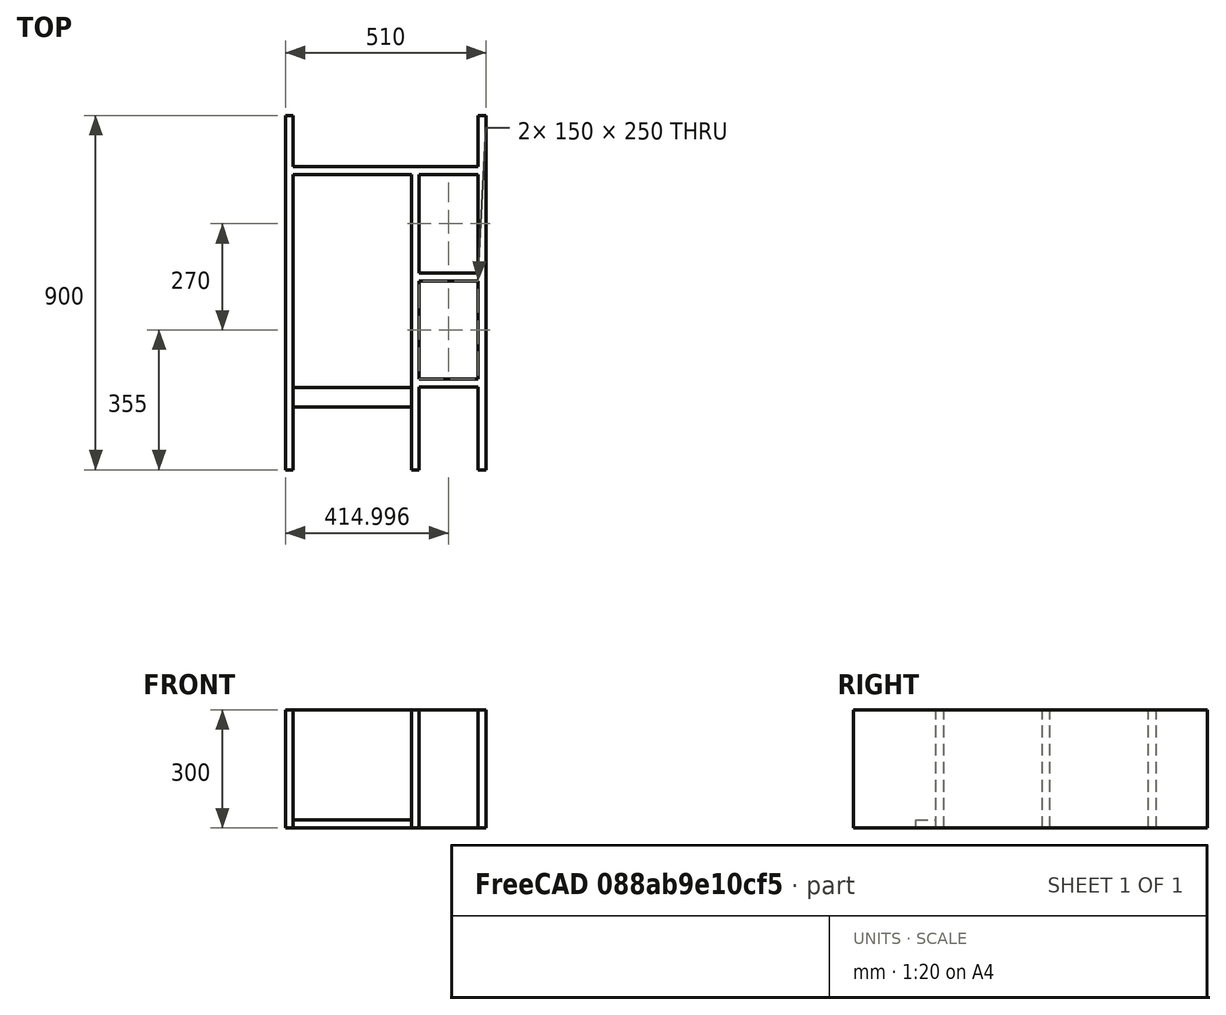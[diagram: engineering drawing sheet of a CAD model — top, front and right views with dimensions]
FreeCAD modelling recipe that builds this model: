
FCSTD DOCUMENT  (FreeCAD 0.18R16110 (Git))
Label: MeubleElodie
License: All rights reserved
LicenseURL: http://en.wikipedia.org/wiki/All_rights_reserved
objects: TechDraw::DrawViewDimension×9, Sketcher::SketchObject×2, PartDesign::Pad×2, TechDraw::DrawSVGTemplate×1, TechDraw::DrawViewAnnotation×1, PartDesign::Body×1, App::Part×1, TechDraw::DrawProjGroupItem×1, TechDraw::DrawProjGroup×1, TechDraw::DrawViewSection×1, TechDraw::DrawViewPart×1, TechDraw::DrawPage×1
note: 7 computed .brp shape members not serialized (recipe doc carries the construction recipe); baked Part::Feature solids carry a one-line shape summary decoded from their .brp

FEATURE [Sketcher::SketchObject] Sketch
  MapMode = 5
  Support = -> [XY_Plane001]
  sketch-geometry (23):
    g0: LineSegment StartX=-287.354 StartY=130 StartZ=0 EndX=-287.354 EndY=-770 EndZ=0
    g1: LineSegment StartX=-287.354 StartY=-770 StartZ=0 EndX=-267.354 EndY=-770 EndZ=0
    g2: LineSegment StartX=-267.354 StartY=-770 StartZ=0 EndX=-267.354 EndY=-20 EndZ=0
    g3: LineSegment StartX=-267.354 StartY=-20 StartZ=0 EndX=32.6459 EndY=-20 EndZ=0
    g4: LineSegment StartX=32.6459 StartY=-20 StartZ=0 EndX=32.6459 EndY=-770 EndZ=0
    g5: LineSegment StartX=32.6459 StartY=-770 StartZ=0 EndX=52.6459 EndY=-770 EndZ=0
    g6: LineSegment StartX=52.6459 StartY=-770 StartZ=0 EndX=52.6459 EndY=-560 EndZ=0
    g7: LineSegment StartX=52.6459 StartY=-20 StartZ=0 EndX=202.646 EndY=-20 EndZ=0
    g8: LineSegment StartX=202.646 StartY=-20 StartZ=0 EndX=202.646 EndY=-770 EndZ=0
    g9: LineSegment StartX=202.646 StartY=-770 StartZ=0 EndX=222.646 EndY=-770 EndZ=0
    g10: LineSegment StartX=222.646 StartY=-770 StartZ=0 EndX=222.646 EndY=130 EndZ=0
    g11: LineSegment StartX=222.646 StartY=130 StartZ=0 EndX=202.646 EndY=130 EndZ=0
    g12: LineSegment StartX=202.646 StartY=130 StartZ=0 EndX=202.646 EndY=0 EndZ=0
    g13: LineSegment StartX=202.646 StartY=0 StartZ=0 EndX=-267.354 EndY=0 EndZ=0
    g14: LineSegment StartX=-267.354 StartY=0 StartZ=0 EndX=-267.354 EndY=130 EndZ=0
    g15: LineSegment StartX=-287.354 StartY=130 StartZ=0 EndX=-267.354 EndY=130 EndZ=0
    g16: LineSegment StartX=52.6459 StartY=-270 StartZ=0 EndX=202.646 EndY=-270 EndZ=0
    g17: LineSegment StartX=202.646 StartY=-290 StartZ=0 EndX=52.6459 EndY=-290 EndZ=0
    g18: LineSegment StartX=52.6459 StartY=-270 StartZ=0 EndX=52.6459 EndY=-20 EndZ=0
    g19: LineSegment StartX=52.6459 StartY=-540 StartZ=0 EndX=202.646 EndY=-540 EndZ=0
    g20: LineSegment StartX=202.646 StartY=-540 StartZ=0 EndX=202.646 EndY=-560 EndZ=0
    g21: LineSegment StartX=202.646 StartY=-560 StartZ=0 EndX=52.6459 EndY=-560 EndZ=0
    g22: LineSegment StartX=52.6459 StartY=-540 StartZ=0 EndX=52.6459 EndY=-290 EndZ=0
  constraints (67):
    c: Coincident(g0,g1)
    c: Coincident(g1,g2)
    c: Vertical(g2)
    c: Coincident(g2,g3)
    c: Horizontal(g3)
    c: Coincident(g3,g4)
    c: Vertical(g4)
    c: Coincident(g4,g5)
    c: Horizontal(g5)
    c: Coincident(g5,g6)
    c: Vertical(g6)
    c: Coincident(g18,g7)
    c: Horizontal(g7)
    c: Coincident(g7,g8)
    c: Vertical(g8)
    c: Coincident(g8,g9)
    c: Horizontal(g9)
    c: Coincident(g9,g10)
    c: Vertical(g10)
    c: Coincident(g10,g11)
    c: Coincident(g11,g12)
    c: PointOnObject(g12,g-1)
    c: Vertical(g12)
    c: Coincident(g12,g13)
    c: PointOnObject(g13,g-1)
    c: Coincident(g13,g14)
    c: Vertical(g14)
    c: Horizontal(g11)
    c: Equal(g14,g12)
    c: Equal(g10,g0)
    c: Equal(g2,g4)
    c: Equal(g4,g8)
    c: DistanceY(g2,g2) = 750
    c: DistanceX(g0,g1) = 20
    c: DistanceY(g7,g12) = 20
    c: Equal(g1,g5)
    c: Equal(g5,g9)
    c: Equal(g9,g11)
    c: DistanceY(g2,g14) = 150
    c: Coincident(g15,g0)
    c: Coincident(g15,g14)
    c: Horizontal(g15)
    c: Equal(g15,g11)
    c: Horizontal(g16)
    c: Horizontal(g17)
    c: DistanceY(g17,g16) = 20
    c: Coincident(g18,g16)
    c: Tangent(g6,g18)
    c: Coincident(g22,g17)
    c: PointOnObject(g16,g8)
    c: PointOnObject(g17,g8)
    c: DistanceY(g2,g13) = 20
    c: DistanceX(g0,g10) = 510
    c: DistanceX(g7,g7) = 150
    c: DistanceY(g16,g7) = 250
    c: Coincident(g19,g20)
    c: Coincident(g20,g21)
    c: Horizontal(g19)
    c: Horizontal(g21)
    c: Vertical(g20)
    c: PointOnObject(g20,g8)
    c: DistanceY(g20,g19) = 20
    c: DistanceY(g19,g17) = 250
    c: PointOnObject(g6,g21)
    c: Coincident(g22,g19)
    c: Tangent(g6,g22)
    c: Parallel(g0,g4)
FEATURE [PartDesign::Pad] Pad
  Length = 300
  Length2 = 100
  Profile = -> Sketch
  Type = 0
FEATURE [TechDraw::DrawSVGTemplate] Template
  EditableTexts = Designed_by_Name=Papa d Elodie; Drawing_number=1.0; FC-Date=29/07/2019; FC-SC=1/10; FC-SH=1; FC-Title=Meuble d Elodie; Subtitle=Subtitle
  Height = 210
  Orientation = 1
  Width = 297
FEATURE [TechDraw::DrawViewAnnotation] Annotation
  Font = osifont
  LineSpace = 80
  LockPosition = false
  MaxWidth = -1
  Rotation = 0
  ScaleType = 0
  Text = 2 - 90x30x2 | 1 - 75x30x2  | 2 - 15x30x2 | 1 - 47x30x2 | 1 - 30x5x2
  TextSize = 5
  TextStyle = 0
  X = 238.236
  Y = 98.3941
FEATURE [Sketcher::SketchObject] Sketch001
  ExternalGeometry = -> [Sketch]
  MapMode = 5
  Support = -> [XY_Plane001]
  sketch-geometry (4):
    g0: LineSegment StartX=-267.354 StartY=-560.446 StartZ=0 EndX=32.6459 EndY=-560.446 EndZ=0
    g1: LineSegment StartX=32.6459 StartY=-560.446 StartZ=0 EndX=32.6459 EndY=-610.446 EndZ=0
    g2: LineSegment StartX=32.6459 StartY=-610.446 StartZ=0 EndX=-267.354 EndY=-610.446 EndZ=0
    g3: LineSegment StartX=-267.354 StartY=-610.446 StartZ=0 EndX=-267.354 EndY=-560.446 EndZ=0
  constraints (11):
    c: Coincident(g0,g1)
    c: Coincident(g1,g2)
    c: Coincident(g2,g3)
    c: Coincident(g3,g0)
    c: Horizontal(g0)
    c: Horizontal(g2)
    c: Vertical(g1)
    c: Vertical(g3)
    c: PointOnObject(g0,g-3)
    c: PointOnObject(g1,g-4)
    c: DistanceY(g1,g1) = 50
FEATURE [PartDesign::Pad] Pad001
  BaseFeature = -> Pad
  Length = 20
  Length2 = 100
  Profile = -> Sketch001
  Type = 0
FEATURE [PartDesign::Body] Body
  Group = -> [Sketch,Pad,Sketch001,Pad001]
  Origin = -> Origin001
  Tip = -> Pad001
FEATURE [App::Part] Part
  Group = -> [Body]
  Origin = -> Origin
FEATURE [TechDraw::DrawProjGroupItem] ProjItem005  label="Front001"
  CoarseView = false
  Direction = (0,0,1)
  Focus = 100
  HardHidden = false
  IsoCount = 0
  IsoHidden = false
  IsoVisible = false
  LockPosition = true
  Perspective = false
  Rotation = 0
  RotationVector = (1,0,0)
  Scale = 0.1
  ScaleType = 2
  SeamHidden = false
  SeamVisible = false
  SmoothHidden = false
  SmoothVisible = false
  Source = -> [Pad001]
  Type = 0
  X = 0
  Y = 0
FEATURE [TechDraw::DrawProjGroup] ProjGroup002
  Anchor = -> ProjItem005
  AutoDistribute = true
  LockPosition = false
  ProjectionType = 0
  Rotation = 0
  Scale = 0.1
  ScaleType = 2
  Source = -> [Pad001]
  Views = -> [ProjItem005]
  X = 67.2245
  Y = 133.567
  spacingX = 15
  spacingY = 15
FEATURE [TechDraw::DrawViewDimension] Dimension
  Arbitrary = false
  FormatSpec = %.2f
  LockPosition = false
  MeasureType = 1
  OverTolerance = 0
  References2D = -> [ProjItem005]
  Rotation = 0
  ScaleType = 0
  Type = 2
  UnderTolerance = 0
  X = -44.8231
  Y = -1.12249
FEATURE [TechDraw::DrawViewDimension] Dimension001
  Arbitrary = false
  FormatSpec = %.2f
  LockPosition = false
  MeasureType = 1
  OverTolerance = 0
  References2D = -> [ProjItem005]
  Rotation = 0
  ScaleType = 0
  Type = 2
  UnderTolerance = 0
  X = -11.9088
  Y = -5.70402
FEATURE [TechDraw::DrawViewDimension] Dimension003
  Arbitrary = false
  FormatSpec = %.2f
  LockPosition = false
  MeasureType = 1
  OverTolerance = 0
  References2D = -> [ProjItem005]
  Rotation = 0
  ScaleType = 0
  Type = 1
  UnderTolerance = 0
  X = -2.69397
  Y = 59.5324
FEATURE [TechDraw::DrawViewDimension] Dimension004
  Arbitrary = false
  FormatSpec = %.2f
  LockPosition = false
  MeasureType = 1
  OverTolerance = 0
  References2D = -> [ProjItem005]
  Rotation = 0
  ScaleType = 0
  Type = 1
  UnderTolerance = 0
  X = -43.2957
  Y = -57.1951
FEATURE [TechDraw::DrawViewDimension] Dimension005
  Arbitrary = false
  FormatSpec = %.2f
  LockPosition = false
  MeasureType = 1
  OverTolerance = 0
  References2D = -> [ProjItem005]
  Rotation = 0
  ScaleType = 0
  Type = 1
  UnderTolerance = 0
  X = -2.05828
  Y = -61.5108
FEATURE [TechDraw::DrawViewDimension] Dimension006
  Arbitrary = false
  FormatSpec = %.2f
  LockPosition = false
  MeasureType = 1
  OverTolerance = 0
  References2D = -> [ProjItem005]
  Rotation = 0
  ScaleType = 0
  Type = 1
  UnderTolerance = 0
  X = 36.9356
  Y = -55.6288
FEATURE [TechDraw::DrawViewSection] Section  label="Section A - A"
  BaseView = -> ProjItem005
  CoarseView = false
  Direction = (-1,0,0)
  Focus = 100
  FuseBeforeCut = true
  HardHidden = false
  HatchScale = 1
  IsoCount = 0
  IsoHidden = false
  IsoVisible = false
  LockPosition = false
  NameGeomPattern = Diamond
  Perspective = false
  Rotation = 90
  Scale = 0.1
  ScaleType = 2
  SeamHidden = false
  SeamVisible = false
  SectionDirection = 0
  SectionNormal = (-1,0,0)
  SectionOrigin = (-32.3541,-320,150)
  SectionSymbol = A
  SmoothHidden = false
  SmoothVisible = false
  Source = -> [Pad001]
  X = 134.632
  Y = 134.077
FEATURE [TechDraw::DrawViewDimension] Dimension007
  Arbitrary = false
  FormatSpec = %.2f
  LockPosition = false
  MeasureType = 1
  OverTolerance = 0
  References2D = -> [Section]
  Rotation = 0
  ScaleType = 0
  Type = 1
  UnderTolerance = 0
  X = 1.20961
  Y = -33.7417
FEATURE [TechDraw::DrawViewDimension] Dimension008
  Arbitrary = false
  FormatSpec = %.2f
  LockPosition = false
  MeasureType = 1
  OverTolerance = 0
  References2D = -> [Section]
  Rotation = 0
  ScaleType = 0
  Type = 2
  UnderTolerance = 0
  X = -27.9859
  Y = -8.87459
FEATURE [TechDraw::DrawViewDimension] Dimension009
  Arbitrary = false
  FormatSpec = %.2f
  LockPosition = false
  MeasureType = 1
  OverTolerance = 0
  References2D = -> [Section]
  Rotation = 0
  ScaleType = 0
  Type = 1
  UnderTolerance = 0
  X = 1.11835
  Y = -55.5125
FEATURE [TechDraw::DrawViewPart] View
  CoarseView = false
  Direction = (0.285,0.113,0.952)
  Focus = 100
  HardHidden = false
  IsoCount = 0
  IsoHidden = false
  IsoVisible = false
  LockPosition = false
  Perspective = false
  Rotation = -78
  Scale = 0.05
  ScaleType = 2
  SeamHidden = false
  SeamVisible = false
  SmoothHidden = false
  SmoothVisible = false
  Source = -> [Pad001]
  X = 239.328
  Y = 168
FEATURE [TechDraw::DrawPage] Page
  KeepUpdated = true
  ProjectionType = 0
  Template = -> Template
  Views = -> [ProjGroup002,Dimension,Dimension001,Dimension003,Dimension004,Annotation,Dimension005,Dimension006,Section,Dimension007,Dimension008,Dimension009,View]
